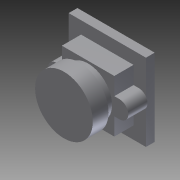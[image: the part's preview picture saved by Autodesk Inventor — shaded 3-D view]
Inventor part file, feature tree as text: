
AUTODESK INVENTOR PART (.ipt)
format: ipt  version: 2011 (Build 150239000, 239)  size: 126,976 bytes
history: native  units: in
note: dims shown in document units (in); Inventor stores cm internally (conversion verified against a paired STEP export)
features: extrude x4, sketch x4
ambient origin geometry x8: Origin, YZ Plane, XZ Plane, XY Plane, X Axis, Y Axis, Z Axis, Center Point
bodies: Solid1 (feature_tree)
feature tree (8):
  extrude  "Extrusion1"  Depth=0.5906in
  extrude  "Extrusion2"  Depth=0.1969in
  extrude  "Extrusion3"  Depth=0.5394in
  extrude  "Extrusion4"  Depth=0.6496in
  sketch  "Sketch1"  dims[d0=0.5906in d1=0.5906in]
  sketch  "Sketch2"  dims[d2=0.1969in d3=0.1969in]
  sketch  "Sketch3"  dims[d4=0.2165in d5=0.0in d6=0.5394in]
  sketch  "Sketch4"  dims[d7=0.0945in d8=0.0in d9=0.6496in d10=0.1772in d11=0.0in d12=0.8701in d13=0.0984in d14=0.0in]
